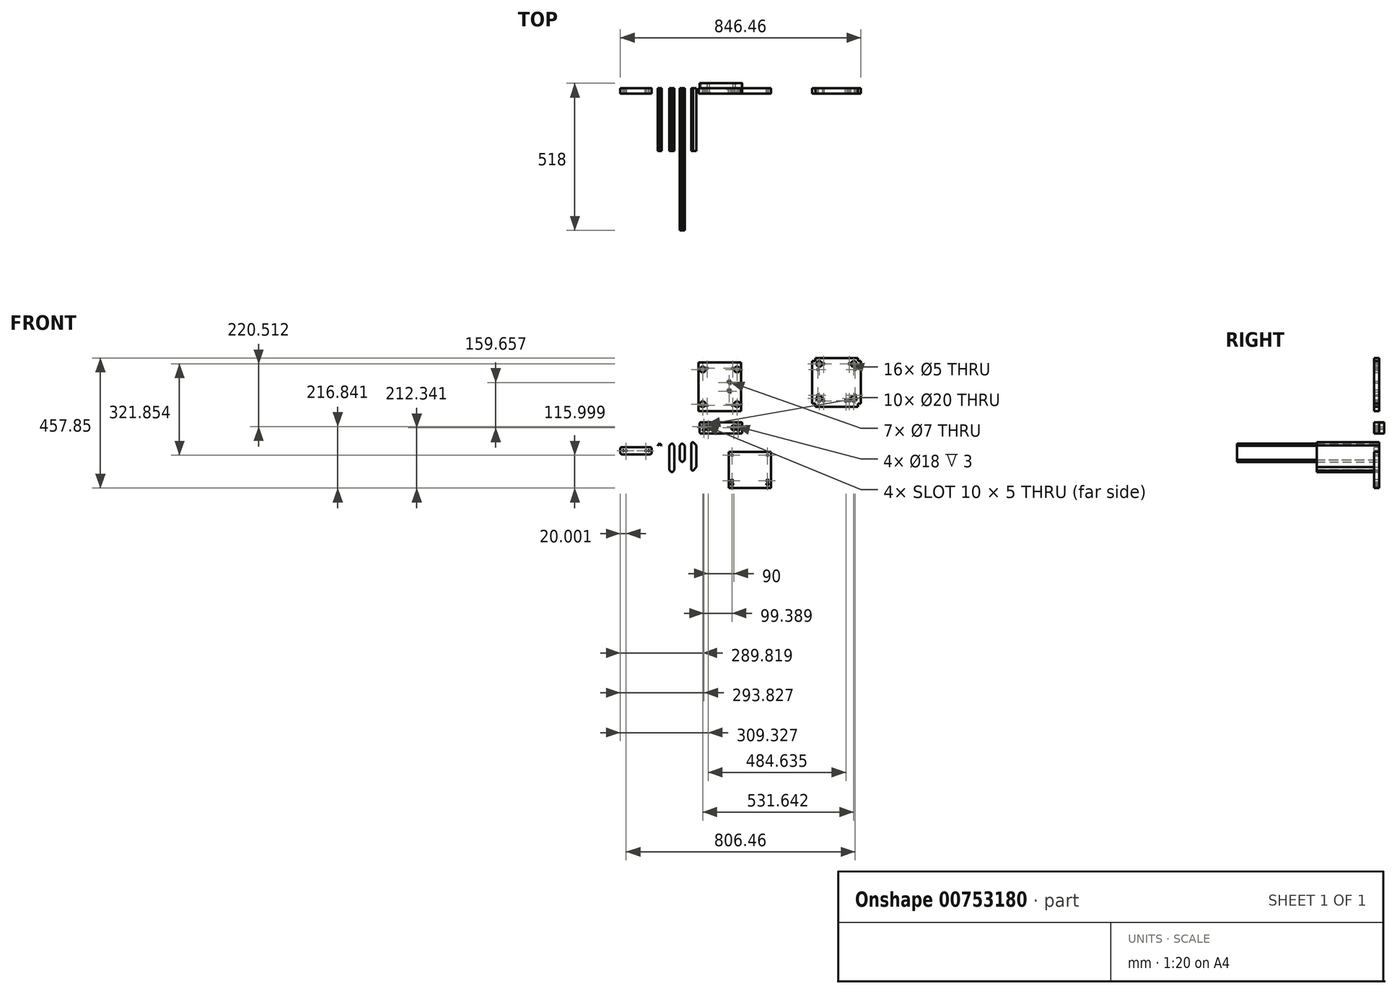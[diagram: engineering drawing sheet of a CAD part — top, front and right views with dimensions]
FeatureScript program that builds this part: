
annotation { "Feature Type Name" : "Feature", "Feature Type Description" : "" }
export const myFeature = defineFeature(function(context is Context, id is Id, definition is map)
    precondition{}
    {
        {
            var Q0;
            Q0=qCreatedBy(makeId("Front.planeOp"),FACE);
            var sketch = newSketch(context, id + "F0", { "sketchPlane" : qUnion([Q0])});
            skLineSegment(sketch, "E0", {"start": v(-1.43, -34.16) * mm, "end": v(-8.96, -26.69) * mm});
            skLineSegment(sketch, "E1", {"start": v(-8.96, -26.69) * mm, "end": v(-8.96, 58.31) * mm});
            skLineSegment(sketch, "E2", {"start": v(-8.96, 58.31) * mm, "end": v(-1.49, 65.84) * mm});
            skLineSegment(sketch, "E3", {"start": v(1.51, 65.84) * mm, "end": v(9.04, 58.37) * mm});
            skLineSegment(sketch, "E4", {"start": v(9.04, 58.37) * mm, "end": v(9.04, -26.63) * mm});
            skLineSegment(sketch, "E5", {"start": v(9.04, -26.63) * mm, "end": v(1.57, -34.16) * mm});
            skLineSegment(sketch, "E6", {"start": v(-1.49, 65.84) * mm, "end": v(1.51, 65.84) * mm});
            skLineSegment(sketch, "E7", {"start": v(-1.43, -34.16) * mm, "end": v(1.57, -34.16) * mm});
            skPoint(sketch, "E8.orphan", {"position": v(0, 67.34) * mm});
            skSolve(sketch);
        }
        {
            var Q0;
            Q0 = qSketchRegion(id + "F0", true);
            extrude(context, id + "F1", {"entities" : qUnion([Q0]), "depth" : 220 * mm, "offsetDistance" : 25 * mm});
        }
        {
            var Q0;
            Q0=qCreatedBy(makeId("Front.planeOp"),FACE);
            var sketch = newSketch(context, id + "F2", { "sketchPlane" : qUnion([Q0])});
            skLineSegment(sketch, "E9", {"start": v(34.52, 0.93) * mm, "end": v(27, 8.4) * mm});
            skLineSegment(sketch, "E10", {"start": v(27, 8.4) * mm, "end": v(27, 58.4) * mm});
            skLineSegment(sketch, "E11", {"start": v(27, 58.4) * mm, "end": v(34.46, 65.93) * mm});
            skLineSegment(sketch, "E12", {"start": v(37.46, 65.93) * mm, "end": v(45, 58.46) * mm});
            skLineSegment(sketch, "E13", {"start": v(45, 58.46) * mm, "end": v(45, 8.46) * mm});
            skLineSegment(sketch, "E14", {"start": v(45, 8.46) * mm, "end": v(37.52, 0.93) * mm});
            skLineSegment(sketch, "E15", {"start": v(34.46, 65.93) * mm, "end": v(37.46, 65.93) * mm});
            skLineSegment(sketch, "E16", {"start": v(34.52, 0.93) * mm, "end": v(37.52, 0.93) * mm});
            skPoint(sketch, "E17.orphan", {"position": v(35.95, 67.43) * mm});
            skSolve(sketch);
        }
        {
            var Q0;
            Q0 = qSketchRegion(id + "F2", true);
            extrude(context, id + "F3", {"entities" : qUnion([Q0]), "depth" : 500 * mm, "offsetDistance" : 25 * mm});
        }
        {
            var Q0;
            Q0=qCreatedBy(makeId("Front.planeOp"),FACE);
            var sketch = newSketch(context, id + "F4", { "sketchPlane" : qUnion([Q0])});
            skLineSegment(sketch, "E18.bottom", {"start": v(-71.5, 28.35) * mm, "end": v(-181.5, 28.35) * mm});
            skLineSegment(sketch, "E18.top", {"start": v(-71.5, 53.35) * mm, "end": v(-181.5, 53.35) * mm});
            skLineSegment(sketch, "E18.left", {"start": v(-71.5, 28.35) * mm, "end": v(-71.5, 53.35) * mm});
            skLineSegment(sketch, "E18.right", {"start": v(-181.5, 28.35) * mm, "end": v(-181.5, 53.35) * mm});
            skCircle(sketch, "E19", {"center": v(-81.5, 40.85) * mm, "radius": 2 * mm});
            skPoint(sketch, "E19.centerSnap0", {"position": v(-71.5, 40.85) * mm});
            skCircle(sketch, "E20", {"center": v(-171.5, 40.85) * mm, "radius": 2 * mm});
            skPoint(sketch, "E20.centerSnap0", {"position": v(-181.5, 40.85) * mm});
            skLineSegment(sketch, "E21", {"start": v(-171.5, 40.85) * mm, "end": v(-181.5, 40.85) * mm, "construction": true});
            skLineSegment(sketch, "E22", {"start": v(-81.5, 40.85) * mm, "end": v(-71.5, 40.85) * mm, "construction": true});
            skLineSegment(sketch, "E23", {"start": v(-171.5, 40.85) * mm, "end": v(-161.5, 40.85) * mm, "construction": true});
            skLineSegment(sketch, "E24", {"start": v(-81.5, 40.85) * mm, "end": v(-91.5, 40.85) * mm, "construction": true});
            skCircle(sketch, "E25", {"center": v(-161.5, 40.85) * mm, "radius": 2.5 * mm});
            skCircle(sketch, "E26", {"center": v(-91.5, 40.85) * mm, "radius": 2.5 * mm});
            skSolve(sketch);
        }
        {
            var Q0;
            Q0 = qSketchRegion(id + "F4", true);
            extrude(context, id + "F5", {"entities" : qUnion([Q0]), "depth" : 18 * mm, "offsetDistance" : 25 * mm});
        }
        {
            var Q0;
            Q0=makeQuery(id+"F5.opExtrude","SWEPT_EDGE",EDGE,{"disambiguationData":[OSD([sQuery(id+"F4.wireOp",EDGE,"E18.top"),sQuery(id+"F4.wireOp",EDGE,"E18.right")])]});
            var Q1;
            Q1=makeQuery(id+"F5.opExtrude","SWEPT_EDGE",EDGE,{"disambiguationData":[OSD([sQuery(id+"F4.wireOp",EDGE,"E18.bottom"),sQuery(id+"F4.wireOp",EDGE,"E18.right")])]});
            var Q2;
            Q2=makeQuery(id+"F5.opExtrude","SWEPT_EDGE",EDGE,{"disambiguationData":[OSD([sQuery(id+"F4.wireOp",EDGE,"E18.top"),sQuery(id+"F4.wireOp",EDGE,"E18.left")])]});
            var Q3;
            Q3=makeQuery(id+"F5.opExtrude","SWEPT_EDGE",EDGE,{"disambiguationData":[OSD([sQuery(id+"F4.wireOp",EDGE,"E18.bottom"),sQuery(id+"F4.wireOp",EDGE,"E18.left")])]});
            fillet(context, id + "F6", {"entities" : qUnion([Q0, Q1, Q2, Q3]), "radius" : 5 * mm, "tangentPropagation" : true, "allowEdgeOverflow" : false});
        }
        {
            var Q0;
            Q0=qCreatedBy(makeId("Front.planeOp"),FACE);
            var sketch = newSketch(context, id + "F7", { "sketchPlane" : qUnion([Q0])});
            skLineSegment(sketch, "E27", {"start": v(-49.39, 58.9) * mm, "end": v(-43.2, 65.1) * mm});
            skLineSegment(sketch, "E28", {"start": v(-43.2, 65.1) * mm, "end": v(-37.01, 58.9) * mm});
            skLineSegment(sketch, "E29", {"start": v(-37.01, 58.9) * mm, "end": v(-36.13, 59.79) * mm});
            skLineSegment(sketch, "E30", {"start": v(-36.13, 59.79) * mm, "end": v(-43.2, 66.86) * mm});
            skLineSegment(sketch, "E31", {"start": v(-43.2, 66.86) * mm, "end": v(-50.27, 59.79) * mm});
            skLineSegment(sketch, "E32", {"start": v(-50.27, 59.79) * mm, "end": v(-49.39, 58.9) * mm});
            skLineSegment(sketch, "E33", {"start": v(-43.2, 65.1) * mm, "end": v(-43.2, 56.01) * mm, "construction": true});
            skSolve(sketch);
        }
        {
            var Q0;
            Q0 = qSketchRegion(id + "F7", true);
            extrude(context, id + "F8", {"entities" : qUnion([Q0]), "depth" : 220 * mm, "offsetDistance" : 25 * mm});
        }
        {
            var Q0;
            Q0=qCreatedBy(makeId("Front.planeOp"),FACE);
            var sketch = newSketch(context, id + "F9", { "sketchPlane" : qUnion([Q0])});
            skLineSegment(sketch, "E34.bottom", {"start": v(199.72, 37.08) * mm, "end": v(348.72, 37.08) * mm});
            skLineSegment(sketch, "E34.left", {"start": v(199.72, 37.08) * mm, "end": v(199.72, -90.92) * mm});
            skLineSegment(sketch, "E34.right", {"start": v(348.72, 37.08) * mm, "end": v(348.72, -90.92) * mm});
            skLineSegment(sketch, "E35", {"start": v(199.76, -19.92) * mm, "end": v(348.76, -19.92) * mm, "construction": true});
            skCircle(sketch, "E36", {"center": v(336.72, 25.08) * mm, "radius": 2.5 * mm});
            skLineSegment(sketch, "E37", {"start": v(211.72, 25.08) * mm, "end": v(199.72, 25.08) * mm, "construction": true});
            skLineSegment(sketch, "E38", {"start": v(336.72, 25.08) * mm, "end": v(348.72, 25.08) * mm, "construction": true});
            skLineSegment(sketch, "E39", {"start": v(211.72, 25.08) * mm, "end": v(211.72, 37.08) * mm, "construction": true});
            skLineSegment(sketch, "E40", {"start": v(336.72, 37.08) * mm, "end": v(336.72, 25.08) * mm, "construction": true});
            skCircle(sketch, "E41", {"center": v(211.72, 25.08) * mm, "radius": 2.5 * mm});
            skCircle(sketch, "E42.MirrorC", {"center": v(336.72, -64.92) * mm, "radius": 2.5 * mm, "construction": true});
            skCircle(sketch, "E43.MirrorC", {"center": v(211.72, -64.92) * mm, "radius": 2.5 * mm, "construction": true});
            skArc(sketch, "E44", {"start": v(214.22, -62.42) * mm, "mid": v(211.72, -59.92) * mm, "end": v(209.22, -62.42) * mm});
            skArc(sketch, "E45", {"start": v(209.22, -67.42) * mm, "mid": v(211.72, -69.92) * mm, "end": v(214.22, -67.42) * mm});
            skLineSegment(sketch, "E46", {"start": v(209.22, -62.42) * mm, "end": v(209.22, -67.42) * mm});
            skLineSegment(sketch, "E47", {"start": v(214.22, -67.42) * mm, "end": v(214.22, -62.42) * mm});
            skLineSegment(sketch, "E48", {"start": v(274.22, 37.08) * mm, "end": v(274.22, -76.92) * mm, "construction": true});
            skLineSegment(sketch, "E49.MirrorCS", {"start": v(339.22, -62.42) * mm, "end": v(339.22, -67.42) * mm});
            skArc(sketch, "E50.MirrorCS", {"start": v(339.22, -67.42) * mm, "mid": v(336.72, -69.92) * mm, "end": v(334.22, -67.42) * mm});
            skLineSegment(sketch, "E51.MirrorCS", {"start": v(334.22, -67.42) * mm, "end": v(334.22, -62.42) * mm});
            skArc(sketch, "E52.MirrorCS", {"start": v(334.22, -62.42) * mm, "mid": v(336.72, -59.92) * mm, "end": v(339.22, -62.42) * mm});
            skArc(sketch, "E53", {"start": v(334.22, -74.92) * mm, "mid": v(332.22, -76.92) * mm, "end": v(334.22, -78.92) * mm});
            skArc(sketch, "E54", {"start": v(339.22, -78.92) * mm, "mid": v(341.22, -76.92) * mm, "end": v(339.22, -74.92) * mm});
            skLineSegment(sketch, "E55", {"start": v(334.22, -76.92) * mm, "end": v(339.22, -76.92) * mm, "construction": true});
            skLineSegment(sketch, "E56", {"start": v(334.22, -74.92) * mm, "end": v(339.22, -74.92) * mm});
            skLineSegment(sketch, "E57", {"start": v(339.22, -78.92) * mm, "end": v(334.22, -78.92) * mm});
            skLineSegment(sketch, "E58", {"start": v(199.72, -90.92) * mm, "end": v(348.72, -90.92) * mm});
            skLineSegment(sketch, "E59", {"start": v(336.72, -69.92) * mm, "end": v(336.72, -74.92) * mm, "construction": true});
            skArc(sketch, "E60.MirrorCS", {"start": v(209.22, -78.92) * mm, "mid": v(207.22, -76.92) * mm, "end": v(209.22, -74.92) * mm});
            skLineSegment(sketch, "E61.MirrorCS", {"start": v(214.22, -74.92) * mm, "end": v(209.22, -74.92) * mm});
            skLineSegment(sketch, "E62.MirrorCS", {"start": v(209.22, -78.92) * mm, "end": v(214.22, -78.92) * mm});
            skArc(sketch, "E63.MirrorCS", {"start": v(214.22, -74.92) * mm, "mid": v(216.22, -76.92) * mm, "end": v(214.22, -78.92) * mm});
            skSolve(sketch);
        }
        {
            var Q0;
            Q0 = qSketchRegion(id + "F9", true);
            extrude(context, id + "F10", {"entities" : qUnion([Q0]), "depth" : 18 * mm, "offsetDistance" : 25 * mm});
        }
        {
            var Q0;
            Q0=makeQuery(id+"F10.opExtrude","SWEPT_FACE",FACE,{"disambiguationData":[OSD([sQuery(id+"F9.wireOp",EDGE,"E58")])]});
            var sketch = newSketch(context, id + "F11", { "sketchPlane" : qUnion([Q0])});
            skCircle(sketch, "E64", {"center": v(211.72, 9) * mm, "radius": 2.5 * mm});
            skPoint(sketch, "E64.centerSnap0", {"position": v(199.72, 9) * mm});
            skCircle(sketch, "E65", {"center": v(336.72, 9) * mm, "radius": 2.5 * mm});
            skPoint(sketch, "E65.centerSnap0", {"position": v(348.72, 9) * mm});
            skSolve(sketch);
        }
        {
            var Q0;
            Q0 = qSketchRegion(id + "F11", true);
            extrude(context, id + "F12", {"entities" : qUnion([Q0]), "operationType" : NewBodyOperationType.REMOVE, "oppositeDirection" : true, "depth" : 25 * mm, "offsetDistance" : 25 * mm});
        }
        {
            var Q0;
            Q0=qCreatedBy(makeId("Front.planeOp"),FACE);
            var sketch = newSketch(context, id + "F13", { "sketchPlane" : qUnion([Q0])});
            skLineSegment(sketch, "E66.left", {"start": v(97.83, 141.42) * mm, "end": v(97.83, 101.42) * mm});
            skLineSegment(sketch, "E67", {"start": v(97.83, 141.42) * mm, "end": v(247.83, 141.42) * mm});
            skCircle(sketch, "E68.MirrorC", {"center": v(233.33, 125.92) * mm, "radius": 2.5 * mm, "construction": true});
            skLineSegment(sketch, "E69.MirrorCS", {"start": v(235.83, 128.42) * mm, "end": v(235.83, 123.42) * mm});
            skArc(sketch, "E70.MirrorCS", {"start": v(235.83, 123.42) * mm, "mid": v(233.33, 120.92) * mm, "end": v(230.83, 123.42) * mm});
            skLineSegment(sketch, "E71.MirrorCS", {"start": v(230.83, 123.42) * mm, "end": v(230.83, 128.42) * mm});
            skArc(sketch, "E72.MirrorCS", {"start": v(230.83, 128.42) * mm, "mid": v(233.33, 130.92) * mm, "end": v(235.83, 128.42) * mm});
            skArc(sketch, "E73", {"start": v(230.83, 115.92) * mm, "mid": v(228.83, 113.92) * mm, "end": v(230.83, 111.92) * mm});
            skArc(sketch, "E74", {"start": v(235.83, 111.92) * mm, "mid": v(237.83, 113.92) * mm, "end": v(235.83, 115.92) * mm});
            skLineSegment(sketch, "E75", {"start": v(230.83, 113.92) * mm, "end": v(235.83, 113.92) * mm, "construction": true});
            skLineSegment(sketch, "E76", {"start": v(230.83, 115.92) * mm, "end": v(235.83, 115.92) * mm});
            skLineSegment(sketch, "E77", {"start": v(235.83, 111.92) * mm, "end": v(230.83, 111.92) * mm});
            skLineSegment(sketch, "E78", {"start": v(97.83, 101.42) * mm, "end": v(247.83, 101.42) * mm});
            skLineSegment(sketch, "E79", {"start": v(233.33, 120.92) * mm, "end": v(233.33, 115.92) * mm, "construction": true});
            skLineSegment(sketch, "E80", {"start": v(247.83, 141.42) * mm, "end": v(247.83, 101.42) * mm});
            skLineSegment(sketch, "E81", {"start": v(172.83, 141.42) * mm, "end": v(172.83, 101.42) * mm, "construction": true});
            skArc(sketch, "E82.MirrorCS", {"start": v(114.83, 115.92) * mm, "mid": v(116.83, 113.92) * mm, "end": v(114.83, 111.92) * mm});
            skLineSegment(sketch, "E83.MirrorCS", {"start": v(109.83, 128.42) * mm, "end": v(109.83, 123.42) * mm});
            skArc(sketch, "E84.MirrorCS", {"start": v(109.83, 123.42) * mm, "mid": v(112.33, 120.92) * mm, "end": v(114.83, 123.42) * mm});
            skLineSegment(sketch, "E85.MirrorCS", {"start": v(114.83, 115.92) * mm, "end": v(109.83, 115.92) * mm});
            skArc(sketch, "E86.MirrorCS", {"start": v(114.83, 128.42) * mm, "mid": v(112.33, 130.92) * mm, "end": v(109.83, 128.42) * mm});
            skLineSegment(sketch, "E87.MirrorCS", {"start": v(109.83, 111.92) * mm, "end": v(114.83, 111.92) * mm});
            skArc(sketch, "E88.MirrorCS", {"start": v(109.83, 111.92) * mm, "mid": v(107.83, 113.92) * mm, "end": v(109.83, 115.92) * mm});
            skLineSegment(sketch, "E89.MirrorCS", {"start": v(114.83, 123.42) * mm, "end": v(114.83, 128.42) * mm});
            skSolve(sketch);
        }
        {
            var Q0;
            Q0 = qSketchRegion(id + "F13", true);
            extrude(context, id + "F14", {"entities" : qUnion([Q0]), "depth" : 18 * mm, "offsetDistance" : 25 * mm});
        }
        {
            var Q0;
            Q0=makeQuery(id+"F14.opExtrude","SWEPT_FACE",FACE,{"disambiguationData":[OSD([sQuery(id+"F13.wireOp",EDGE,"E78")])]});
            var sketch = newSketch(context, id + "F15", { "sketchPlane" : qUnion([Q0])});
            skCircle(sketch, "E90", {"center": v(112.33, 9) * mm, "radius": 2.5 * mm});
            skPoint(sketch, "E90.centerSnap0", {"position": v(97.83, 9) * mm});
            skLineSegment(sketch, "E91", {"start": v(172.83, 18) * mm, "end": v(172.83, 0) * mm, "construction": true});
            skCircle(sketch, "E92.MirrorC", {"center": v(233.33, 9) * mm, "radius": 2.5 * mm});
            skSolve(sketch);
        }
        {
            var Q0;
            Q0 = qSketchRegion(id + "F15", true);
            extrude(context, id + "F16", {"entities" : qUnion([Q0]), "operationType" : NewBodyOperationType.REMOVE, "oppositeDirection" : true, "depth" : 25 * mm, "offsetDistance" : 25 * mm});
        }
        {
            var Q0;
            Q0=makeQuery(id+"F14.opExtrude","SWEPT_EDGE",EDGE,{"disambiguationData":[OSD([sQuery(id+"F13.wireOp",EDGE,"E66.left"),sQuery(id+"F13.wireOp",EDGE,"E67")])]});
            var Q1;
            Q1=makeQuery(id+"F14.opExtrude","SWEPT_EDGE",EDGE,{"disambiguationData":[OSD([sQuery(id+"F13.wireOp",EDGE,"E66.left"),sQuery(id+"F13.wireOp",EDGE,"E78")])]});
            var Q2;
            Q2=makeQuery(id+"F14.opExtrude","SWEPT_EDGE",EDGE,{"disambiguationData":[OSD([sQuery(id+"F13.wireOp",EDGE,"E78"),sQuery(id+"F13.wireOp",EDGE,"E80")])]});
            var Q3;
            Q3=makeQuery(id+"F14.opExtrude","SWEPT_EDGE",EDGE,{"disambiguationData":[OSD([sQuery(id+"F13.wireOp",EDGE,"E67"),sQuery(id+"F13.wireOp",EDGE,"E80")])]});
            fillet(context, id + "F17", {"entities" : qUnion([Q0, Q1, Q2, Q3]), "radius" : 5 * mm, "tangentPropagation" : true, "allowEdgeOverflow" : false});
        }
        {
            var Q0;
            Q0=makeQuery(id+"F14.opExtrude","CAP_FACE",FACE,{"disambiguationData":[OSD([sQuery(id+"F13.wireOp",EDGE,"E66.left"),sQuery(id+"F13.wireOp",EDGE,"E67"),sQuery(id+"F13.wireOp",EDGE,"E69.MirrorCS"),sQuery(id+"F13.wireOp",EDGE,"E70.MirrorCS"),sQuery(id+"F13.wireOp",EDGE,"E71.MirrorCS"),sQuery(id+"F13.wireOp",EDGE,"E72.MirrorCS"),sQuery(id+"F13.wireOp",EDGE,"E73"),sQuery(id+"F13.wireOp",EDGE,"E74"),sQuery(id+"F13.wireOp",EDGE,"E76"),sQuery(id+"F13.wireOp",EDGE,"E77"),sQuery(id+"F13.wireOp",EDGE,"E78"),sQuery(id+"F13.wireOp",EDGE,"E80"),sQuery(id+"F13.wireOp",EDGE,"E82.MirrorCS"),sQuery(id+"F13.wireOp",EDGE,"E83.MirrorCS"),sQuery(id+"F13.wireOp",EDGE,"E84.MirrorCS"),sQuery(id+"F13.wireOp",EDGE,"E85.MirrorCS"),sQuery(id+"F13.wireOp",EDGE,"E86.MirrorCS"),sQuery(id+"F13.wireOp",EDGE,"E87.MirrorCS"),sQuery(id+"F13.wireOp",EDGE,"E88.MirrorCS"),sQuery(id+"F13.wireOp",EDGE,"E89.MirrorCS")])],"isStart":false});
            var sketch = newSketch(context, id + "F18", { "sketchPlane" : qUnion([Q0])});
            skCircle(sketch, "E93", {"center": v(127.83, 121.42) * mm, "radius": 3.5 * mm});
            skPoint(sketch, "E93.centerSnap0", {"position": v(97.83, 121.42) * mm});
            skLineSegment(sketch, "E94", {"start": v(172.83, 141.42) * mm, "end": v(172.83, 101.42) * mm, "construction": true});
            skCircle(sketch, "E95.MirrorC", {"center": v(217.83, 121.42) * mm, "radius": 3.5 * mm});
            skSolve(sketch);
        }
        {
            var Q0;
            Q0 = qSketchRegion(id + "F18", true);
            extrude(context, id + "F19", {"entities" : qUnion([Q0]), "operationType" : NewBodyOperationType.REMOVE, "oppositeDirection" : true, "depth" : 25 * mm, "offsetDistance" : 25 * mm});
        }
        {
            var Q0;
            Q0=makeQuery(id+"F14.opExtrude","CAP_FACE",FACE,{"disambiguationData":[OSD([sQuery(id+"F13.wireOp",EDGE,"E66.left"),sQuery(id+"F13.wireOp",EDGE,"E67"),sQuery(id+"F13.wireOp",EDGE,"E69.MirrorCS"),sQuery(id+"F13.wireOp",EDGE,"E70.MirrorCS"),sQuery(id+"F13.wireOp",EDGE,"E71.MirrorCS"),sQuery(id+"F13.wireOp",EDGE,"E72.MirrorCS"),sQuery(id+"F13.wireOp",EDGE,"E73"),sQuery(id+"F13.wireOp",EDGE,"E74"),sQuery(id+"F13.wireOp",EDGE,"E76"),sQuery(id+"F13.wireOp",EDGE,"E77"),sQuery(id+"F13.wireOp",EDGE,"E78"),sQuery(id+"F13.wireOp",EDGE,"E80"),sQuery(id+"F13.wireOp",EDGE,"E82.MirrorCS"),sQuery(id+"F13.wireOp",EDGE,"E83.MirrorCS"),sQuery(id+"F13.wireOp",EDGE,"E84.MirrorCS"),sQuery(id+"F13.wireOp",EDGE,"E85.MirrorCS"),sQuery(id+"F13.wireOp",EDGE,"E86.MirrorCS"),sQuery(id+"F13.wireOp",EDGE,"E87.MirrorCS"),sQuery(id+"F13.wireOp",EDGE,"E88.MirrorCS"),sQuery(id+"F13.wireOp",EDGE,"E89.MirrorCS")])],"isStart":false});
            var sketch = newSketch(context, id + "F20", { "sketchPlane" : qUnion([Q0])});
            skCircle(sketch, "E96", {"center": v(127.83, 121.42) * mm, "radius": 9 * mm});
            skCircle(sketch, "E97", {"center": v(217.83, 121.42) * mm, "radius": 9 * mm});
            skSolve(sketch);
        }
        {
            var Q0;
            Q0 = qSketchRegion(id + "F20", true);
            extrude(context, id + "F21", {"entities" : qUnion([Q0]), "operationType" : NewBodyOperationType.REMOVE, "oppositeDirection" : true, "depth" : 3 * mm, "offsetDistance" : 25 * mm});
        }
        {
            var Q0;
            Q0=qCreatedBy(makeId("Front.planeOp"),FACE);
            var sketch = newSketch(context, id + "F22", { "sketchPlane" : qUnion([Q0])});
            skLineSegment(sketch, "E98.bottom", {"start": v(93.82, 180.08) * mm, "end": v(243.82, 180.08) * mm});
            skLineSegment(sketch, "E98.top", {"start": v(93.82, 351.08) * mm, "end": v(243.82, 351.08) * mm});
            skLineSegment(sketch, "E98.left", {"start": v(93.82, 180.08) * mm, "end": v(93.82, 351.08) * mm});
            skLineSegment(sketch, "E98.right", {"start": v(243.82, 180.08) * mm, "end": v(243.82, 351.08) * mm});
            skLineSegment(sketch, "E99", {"start": v(93.82, 220.08) * mm, "end": v(243.82, 220.08) * mm, "construction": true});
            skLineSegment(sketch, "E100", {"start": v(93.82, 311.08) * mm, "end": v(243.82, 311.08) * mm, "construction": true});
            skLineSegment(sketch, "E101", {"start": v(93.82, 326.08) * mm, "end": v(243.82, 326.08) * mm, "construction": true});
            skLineSegment(sketch, "E102", {"start": v(93.82, 205.08) * mm, "end": v(243.82, 205.08) * mm, "construction": true});
            skLineSegment(sketch, "E103", {"start": v(93.82, 200.08) * mm, "end": v(168.82, 200.08) * mm, "construction": true});
            skPoint(sketch, "E103.endSnap0", {"position": v(168.82, 180.08) * mm});
            skCircle(sketch, "E104", {"center": v(123.82, 200.08) * mm, "radius": 2.5 * mm});
            skLineSegment(sketch, "E105", {"start": v(168.82, 200.08) * mm, "end": v(168.82, 180.08) * mm, "construction": true});
            skCircle(sketch, "E106.MirrorC", {"center": v(213.82, 200.08) * mm, "radius": 2.5 * mm});
            skLineSegment(sketch, "E107", {"start": v(93.82, 265.58) * mm, "end": v(243.82, 265.58) * mm, "construction": true});
            skCircle(sketch, "E108.MirrorC", {"center": v(213.82, 331.08) * mm, "radius": 2.5 * mm});
            skCircle(sketch, "E109.MirrorC", {"center": v(123.82, 331.08) * mm, "radius": 2.5 * mm});
            skSolve(sketch);
        }
        {
            var Q0;
            Q0 = qSketchRegion(id + "F22", true);
            extrude(context, id + "F23", {"entities" : qUnion([Q0]), "depth" : 18 * mm, "offsetDistance" : 25 * mm});
        }
        {
            var Q0;
            Q0=makeQuery(id+"F23.opExtrude","CAP_FACE",FACE,{"disambiguationData":[OSD([sQuery(id+"F22.wireOp",EDGE,"E98.bottom"),sQuery(id+"F22.wireOp",EDGE,"E98.top"),sQuery(id+"F22.wireOp",EDGE,"E98.left"),sQuery(id+"F22.wireOp",EDGE,"E98.right"),sQuery(id+"F22.wireOp",EDGE,"E104"),sQuery(id+"F22.wireOp",EDGE,"E106.MirrorC"),sQuery(id+"F22.wireOp",EDGE,"E108.MirrorC"),sQuery(id+"F22.wireOp",EDGE,"E109.MirrorC")])],"isStart":true});
            var sketch = newSketch(context, id + "F24", { "sketchPlane" : qUnion([Q0])});
            skLineSegment(sketch, "E110", {"start": v(-168.82, 220.08) * mm, "end": v(-168.82, 180.08) * mm, "construction": true});
            skCircle(sketch, "E111", {"center": v(-108.32, 204.58) * mm, "radius": 10 * mm});
            skCircle(sketch, "E112.MirrorC", {"center": v(-229.32, 204.58) * mm, "radius": 10 * mm});
            skLineSegment(sketch, "E113", {"start": v(-243.82, 265.58) * mm, "end": v(-159.86, 265.58) * mm, "construction": true});
            skCircle(sketch, "E114.MirrorC", {"center": v(-108.32, 326.58) * mm, "radius": 10 * mm});
            skCircle(sketch, "E115.MirrorC", {"center": v(-229.32, 326.58) * mm, "radius": 10 * mm});
            skSolve(sketch);
        }
        {
            var Q0;
            Q0 = qSketchRegion(id + "F24", true);
            extrude(context, id + "F25", {"entities" : qUnion([Q0]), "operationType" : NewBodyOperationType.REMOVE, "oppositeDirection" : true, "depth" : 25 * mm, "offsetDistance" : 25 * mm});
        }
        {
            var Q0;
            Q0=makeQuery(id+"F23.opExtrude","CAP_FACE",FACE,{"disambiguationData":[OSD([sQuery(id+"F22.wireOp",EDGE,"E98.bottom"),sQuery(id+"F22.wireOp",EDGE,"E98.top"),sQuery(id+"F22.wireOp",EDGE,"E98.left"),sQuery(id+"F22.wireOp",EDGE,"E98.right"),sQuery(id+"F22.wireOp",EDGE,"E104"),sQuery(id+"F22.wireOp",EDGE,"E106.MirrorC"),sQuery(id+"F22.wireOp",EDGE,"E108.MirrorC"),sQuery(id+"F22.wireOp",EDGE,"E109.MirrorC")])],"isStart":false});
            var sketch = newSketch(context, id + "F26", { "sketchPlane" : qUnion([Q0])});
            skLineSegment(sketch, "E116", {"start": v(93.82, 265.58) * mm, "end": v(201.82, 265.58) * mm, "construction": true});
            skLineSegment(sketch, "E117", {"start": v(201.82, 281.08) * mm, "end": v(201.82, 250.08) * mm, "construction": true});
            skCircle(sketch, "E118", {"center": v(201.82, 281.08) * mm, "radius": 3.5 * mm});
            skCircle(sketch, "E119", {"center": v(201.82, 250.08) * mm, "radius": 3.5 * mm});
            skSolve(sketch);
        }
        {
            var Q0;
            Q0 = qSketchRegion(id + "F26", true);
            extrude(context, id + "F27", {"entities" : qUnion([Q0]), "operationType" : NewBodyOperationType.REMOVE, "oppositeDirection" : true, "depth" : 25 * mm, "offsetDistance" : 25 * mm});
        }
        {
            var Q0;
            Q0=makeQuery(id+"F23.opExtrude","CAP_FACE",FACE,{"disambiguationData":[OSD([sQuery(id+"F22.wireOp",EDGE,"E98.bottom"),sQuery(id+"F22.wireOp",EDGE,"E98.top"),sQuery(id+"F22.wireOp",EDGE,"E98.left"),sQuery(id+"F22.wireOp",EDGE,"E98.right"),sQuery(id+"F22.wireOp",EDGE,"E104"),sQuery(id+"F22.wireOp",EDGE,"E106.MirrorC"),sQuery(id+"F22.wireOp",EDGE,"E108.MirrorC"),sQuery(id+"F22.wireOp",EDGE,"E109.MirrorC")])],"isStart":true});
            var sketch = newSketch(context, id + "F28", { "sketchPlane" : qUnion([Q0])});
            skCircle(sketch, "E120", {"center": v(-201.82, 281.08) * mm, "radius": 9 * mm});
            skCircle(sketch, "E121", {"center": v(-201.82, 250.08) * mm, "radius": 9 * mm});
            skSolve(sketch);
        }
        {
            var Q0;
            Q0 = qSketchRegion(id + "F28", true);
            extrude(context, id + "F29", {"entities" : qUnion([Q0]), "operationType" : NewBodyOperationType.REMOVE, "oppositeDirection" : true, "depth" : 3 * mm, "offsetDistance" : 25 * mm});
        }
        {
            var Q0;
            Q0=makeQuery(id+"F14.opExtrude","CAP_FACE",FACE,{"disambiguationData":[OSD([sQuery(id+"F13.wireOp",EDGE,"E66.left"),sQuery(id+"F13.wireOp",EDGE,"E67"),sQuery(id+"F13.wireOp",EDGE,"E69.MirrorCS"),sQuery(id+"F13.wireOp",EDGE,"E70.MirrorCS"),sQuery(id+"F13.wireOp",EDGE,"E71.MirrorCS"),sQuery(id+"F13.wireOp",EDGE,"E72.MirrorCS"),sQuery(id+"F13.wireOp",EDGE,"E73"),sQuery(id+"F13.wireOp",EDGE,"E74"),sQuery(id+"F13.wireOp",EDGE,"E76"),sQuery(id+"F13.wireOp",EDGE,"E77"),sQuery(id+"F13.wireOp",EDGE,"E78"),sQuery(id+"F13.wireOp",EDGE,"E80"),sQuery(id+"F13.wireOp",EDGE,"E82.MirrorCS"),sQuery(id+"F13.wireOp",EDGE,"E83.MirrorCS"),sQuery(id+"F13.wireOp",EDGE,"E84.MirrorCS"),sQuery(id+"F13.wireOp",EDGE,"E85.MirrorCS"),sQuery(id+"F13.wireOp",EDGE,"E86.MirrorCS"),sQuery(id+"F13.wireOp",EDGE,"E87.MirrorCS"),sQuery(id+"F13.wireOp",EDGE,"E88.MirrorCS"),sQuery(id+"F13.wireOp",EDGE,"E89.MirrorCS")])],"isStart":true});
            var sketch = newSketch(context, id + "F30", { "sketchPlane" : qUnion([Q0])});
            skArc(sketch, "E122.0", {"start": v(-97.83, 136.42) * mm, "mid": v(-99.3, 139.96) * mm, "end": v(-102.83, 141.42) * mm});
            skLineSegment(sketch, "E122.1", {"start": v(-97.83, 106.42) * mm, "end": v(-97.83, 136.42) * mm});
            skLineSegment(sketch, "E122.2", {"start": v(-102.83, 141.42) * mm, "end": v(-242.83, 141.42) * mm});
            skArc(sketch, "E122.3", {"start": v(-102.83, 101.42) * mm, "mid": v(-99.3, 102.89) * mm, "end": v(-97.83, 106.42) * mm});
            skArc(sketch, "E122.4", {"start": v(-242.83, 141.42) * mm, "mid": v(-246.36, 139.96) * mm, "end": v(-247.83, 136.42) * mm});
            skLineSegment(sketch, "E122.5", {"start": v(-247.83, 136.42) * mm, "end": v(-247.83, 106.42) * mm});
            skArc(sketch, "E122.6", {"start": v(-247.83, 106.42) * mm, "mid": v(-246.36, 102.89) * mm, "end": v(-242.83, 101.42) * mm});
            skLineSegment(sketch, "E122.7", {"start": v(-242.83, 101.42) * mm, "end": v(-102.83, 101.42) * mm});
            skCircle(sketch, "E123", {"center": v(-217.83, 121.42) * mm, "radius": 3.5 * mm});
            skCircle(sketch, "E124", {"center": v(-127.83, 121.42) * mm, "radius": 3.5 * mm});
            skCircle(sketch, "E125", {"center": v(-233.33, 125.92) * mm, "radius": 10 * mm});
            skPoint(sketch, "E125.centerSnap0", {"position": v(-233.33, 130.92) * mm});
            skPoint(sketch, "E125.centerSnap1", {"position": v(-230.83, 125.92) * mm});
            skCircle(sketch, "E126", {"center": v(-112.33, 125.92) * mm, "radius": 10 * mm});
            skPoint(sketch, "E126.centerSnap0", {"position": v(-109.83, 125.92) * mm});
            skPoint(sketch, "E126.centerSnap1", {"position": v(-112.33, 130.92) * mm});
            skSolve(sketch);
        }
        {
            var Q0;
            Q0 = qSketchRegion(id + "F30", true);
            extrude(context, id + "F31", {"entities" : qUnion([Q0]), "depth" : 18 * mm, "offsetDistance" : 25 * mm});
        }
        {
            var Q0;
            Q0=qCreatedBy(makeId("Front.planeOp"),FACE);
            var sketch = newSketch(context, id + "F32", { "sketchPlane" : qUnion([Q0])});
            skLineSegment(sketch, "E127", {"start": v(72.31, -28.94) * mm, "end": v(68.31, -24.94) * mm});
            skLineSegment(sketch, "E128", {"start": v(68.31, -24.94) * mm, "end": v(68.31, 67.06) * mm});
            skLineSegment(sketch, "E129", {"start": v(68.31, 67.06) * mm, "end": v(72.31, 71.06) * mm});
            skLineSegment(sketch, "E130", {"start": v(74.31, 71.06) * mm, "end": v(86.31, 59.06) * mm});
            skLineSegment(sketch, "E131", {"start": v(86.31, 59.06) * mm, "end": v(86.31, -16.94) * mm});
            skLineSegment(sketch, "E132", {"start": v(86.31, -16.94) * mm, "end": v(74.31, -28.94) * mm});
            skLineSegment(sketch, "E133", {"start": v(72.31, 71.06) * mm, "end": v(74.31, 71.06) * mm});
            skLineSegment(sketch, "E134", {"start": v(72.31, -28.94) * mm, "end": v(74.31, -28.94) * mm});
            skPoint(sketch, "E135.orphan", {"position": v(73.31, 72.06) * mm});
            skSolve(sketch);
        }
        {
            var Q0;
            Q0 = qSketchRegion(id + "F32", true);
            extrude(context, id + "F33", {"entities" : qUnion([Q0]), "depth" : 220 * mm, "offsetDistance" : 25 * mm});
        }
        {
            var Q0;
            Q0=qCreatedBy(makeId("Front.planeOp"),FACE);
            var sketch = newSketch(context, id + "F34", { "sketchPlane" : qUnion([Q0])});
            skLineSegment(sketch, "E136.bottom", {"start": v(504.46, 195.93) * mm, "end": v(654.46, 195.93) * mm});
            skLineSegment(sketch, "E136.top", {"start": v(504.46, 366.93) * mm, "end": v(654.46, 366.93) * mm});
            skLineSegment(sketch, "E136.left", {"start": v(504.46, 195.93) * mm, "end": v(504.46, 366.93) * mm});
            skLineSegment(sketch, "E136.right", {"start": v(654.46, 195.93) * mm, "end": v(654.46, 366.93) * mm});
            skLineSegment(sketch, "E137", {"start": v(504.46, 235.93) * mm, "end": v(654.46, 235.93) * mm, "construction": true});
            skLineSegment(sketch, "E138", {"start": v(504.46, 326.93) * mm, "end": v(654.46, 326.93) * mm, "construction": true});
            skLineSegment(sketch, "E139", {"start": v(504.46, 341.93) * mm, "end": v(654.46, 341.93) * mm, "construction": true});
            skLineSegment(sketch, "E140", {"start": v(504.46, 220.93) * mm, "end": v(654.46, 220.93) * mm, "construction": true});
            skLineSegment(sketch, "E141", {"start": v(504.46, 215.93) * mm, "end": v(579.46, 215.93) * mm, "construction": true});
            skPoint(sketch, "E141.endSnap0", {"position": v(579.46, 195.93) * mm});
            skCircle(sketch, "E142", {"center": v(534.46, 215.93) * mm, "radius": 2.5 * mm});
            skLineSegment(sketch, "E143", {"start": v(579.46, 215.93) * mm, "end": v(579.46, 195.93) * mm, "construction": true});
            skCircle(sketch, "E144.MirrorC", {"center": v(624.46, 215.93) * mm, "radius": 2.5 * mm});
            skLineSegment(sketch, "E145", {"start": v(504.46, 281.43) * mm, "end": v(654.46, 281.43) * mm, "construction": true});
            skCircle(sketch, "E146.MirrorC", {"center": v(624.46, 346.93) * mm, "radius": 2.5 * mm});
            skCircle(sketch, "E147.MirrorC", {"center": v(534.46, 346.93) * mm, "radius": 2.5 * mm});
            skLineSegment(sketch, "E148.bottom", {"start": v(664.96, 206.43) * mm, "end": v(664.96, 356.43) * mm});
            skLineSegment(sketch, "E148.top", {"start": v(493.96, 206.43) * mm, "end": v(493.96, 356.43) * mm});
            skLineSegment(sketch, "E148.left", {"start": v(664.96, 206.43) * mm, "end": v(493.96, 206.43) * mm});
            skLineSegment(sketch, "E148.right", {"start": v(664.96, 356.43) * mm, "end": v(493.96, 356.43) * mm});
            skLineSegment(sketch, "E149", {"start": v(624.96, 206.43) * mm, "end": v(624.96, 356.43) * mm, "construction": true});
            skLineSegment(sketch, "E150", {"start": v(533.96, 206.43) * mm, "end": v(533.96, 356.43) * mm, "construction": true});
            skLineSegment(sketch, "E151", {"start": v(518.96, 206.43) * mm, "end": v(518.96, 356.43) * mm, "construction": true});
            skLineSegment(sketch, "E152", {"start": v(639.96, 206.43) * mm, "end": v(639.96, 356.43) * mm, "construction": true});
            skLineSegment(sketch, "E153", {"start": v(644.96, 206.43) * mm, "end": v(644.96, 281.43) * mm, "construction": true});
            skPoint(sketch, "E153.endSnap0", {"position": v(664.96, 281.43) * mm});
            skCircle(sketch, "E154", {"center": v(644.96, 236.43) * mm, "radius": 2.5 * mm});
            skLineSegment(sketch, "E155", {"start": v(644.96, 281.43) * mm, "end": v(664.96, 281.43) * mm, "construction": true});
            skCircle(sketch, "E156.MirrorC", {"center": v(644.96, 326.43) * mm, "radius": 2.5 * mm});
            skLineSegment(sketch, "E157", {"start": v(579.46, 206.43) * mm, "end": v(579.46, 356.43) * mm, "construction": true});
            skCircle(sketch, "E158.MirrorC", {"center": v(513.96, 326.43) * mm, "radius": 2.5 * mm});
            skCircle(sketch, "E159.MirrorC", {"center": v(513.96, 236.43) * mm, "radius": 2.5 * mm});
            skPoint(sketch, "E160", {"position": v(579.46, 281.43) * mm});
            skSolve(sketch);
        }
        {
            var Q0;
            Q0 = qSketchRegion(id + "F34", true);
            extrude(context, id + "F35", {"entities" : qUnion([Q0]), "depth" : 18 * mm, "offsetDistance" : 25 * mm});
        }
        {
            var Q0;
            Q0=makeQuery(id+"F35.opExtrude","CAP_FACE",FACE,{"disambiguationData":[OSD([sQuery(id+"F34.wireOp",EDGE,"E136.bottom"),sQuery(id+"F34.wireOp",EDGE,"E136.top"),sQuery(id+"F34.wireOp",EDGE,"E136.left"),sQuery(id+"F34.wireOp",EDGE,"E136.right"),sQuery(id+"F34.wireOp",EDGE,"E142"),sQuery(id+"F34.wireOp",EDGE,"E144.MirrorC"),sQuery(id+"F34.wireOp",EDGE,"E146.MirrorC"),sQuery(id+"F34.wireOp",EDGE,"E147.MirrorC")])],"isStart":false});
            var sketch = newSketch(context, id + "F36", { "sketchPlane" : qUnion([Q0])});
            skLineSegment(sketch, "E161", {"start": v(579.46, 235.93) * mm, "end": v(579.46, 195.93) * mm, "construction": true});
            skCircle(sketch, "E162", {"center": v(639.96, 224.43) * mm, "radius": 10 * mm});
            skCircle(sketch, "E163.MirrorC", {"center": v(518.96, 224.43) * mm, "radius": 10 * mm});
            skLineSegment(sketch, "E164", {"start": v(504.46, 285.43) * mm, "end": v(588.42, 285.43) * mm, "construction": true});
            skCircle(sketch, "E165.MirrorC", {"center": v(639.96, 346.43) * mm, "radius": 10 * mm});
            skCircle(sketch, "E166.MirrorC", {"center": v(518.96, 346.43) * mm, "radius": 10 * mm});
            skPoint(sketch, "E167", {"position": v(579.46, 195.93) * mm});
            skSolve(sketch);
        }
        {
            var Q0;
            Q0 = qSketchRegion(id + "F36", true);
            extrude(context, id + "F37", {"entities" : qUnion([Q0]), "operationType" : NewBodyOperationType.REMOVE, "oppositeDirection" : true, "depth" : 25 * mm, "offsetDistance" : 25 * mm});
        }
        {
            var Q0;
            Q0=makeQuery(id+"F35.opExtrude","CAP_FACE",FACE,{"disambiguationData":[OSD([sQuery(id+"F34.wireOp",EDGE,"E136.bottom"),sQuery(id+"F34.wireOp",EDGE,"E136.top"),sQuery(id+"F34.wireOp",EDGE,"E136.left"),sQuery(id+"F34.wireOp",EDGE,"E136.right"),sQuery(id+"F34.wireOp",EDGE,"E142"),sQuery(id+"F34.wireOp",EDGE,"E144.MirrorC"),sQuery(id+"F34.wireOp",EDGE,"E146.MirrorC"),sQuery(id+"F34.wireOp",EDGE,"E147.MirrorC")])],"isStart":false});
            var sketch = newSketch(context, id + "F38", { "sketchPlane" : qUnion([Q0])});
            skLineSegment(sketch, "E168", {"start": v(504.46, 201.18) * mm, "end": v(612.46, 201.18) * mm, "construction": true});
            skLineSegment(sketch, "E169", {"start": v(612.46, 216.68) * mm, "end": v(612.46, 185.68) * mm, "construction": true});
            skCircle(sketch, "E170", {"center": v(612.46, 216.68) * mm, "radius": 3.5 * mm});
            skCircle(sketch, "E171", {"center": v(612.46, 185.68) * mm, "radius": 3.5 * mm});
            skSolve(sketch);
        }
        {
            var Q0;
            Q0 = qSketchRegion(id + "F38", true);
            extrude(context, id + "F39", {"entities" : qUnion([Q0]), "operationType" : NewBodyOperationType.REMOVE, "oppositeDirection" : true, "depth" : 25 * mm, "offsetDistance" : 25 * mm});
        }
    });
